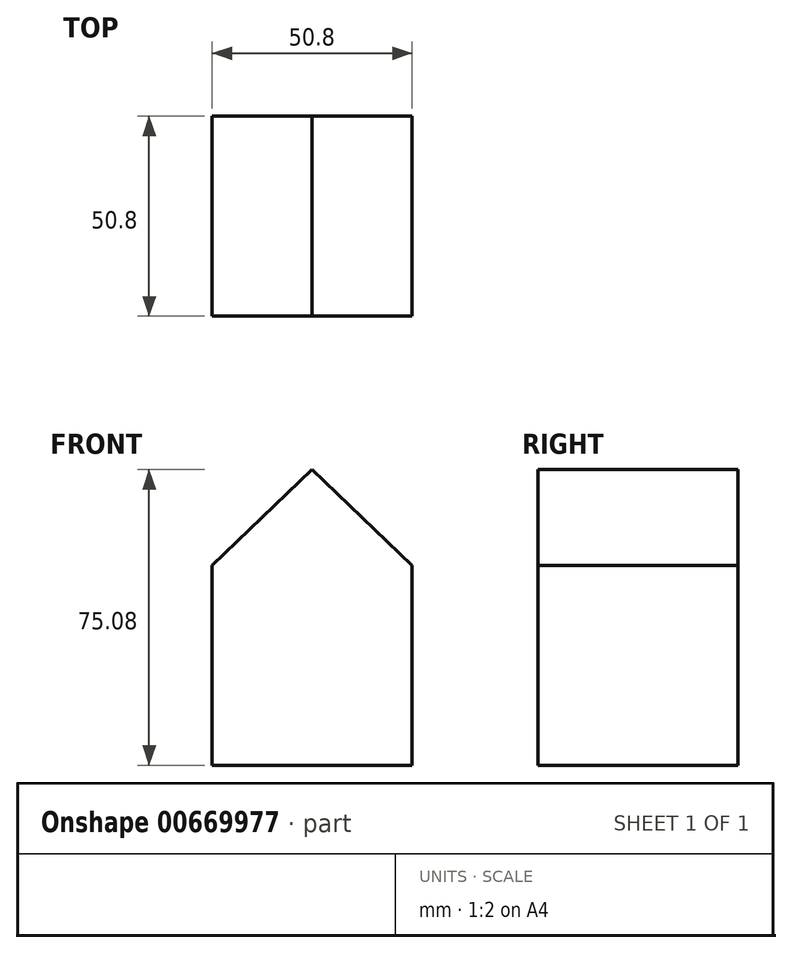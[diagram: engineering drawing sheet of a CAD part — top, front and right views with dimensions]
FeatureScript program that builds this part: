
annotation { "Feature Type Name" : "Feature", "Feature Type Description" : "" }
export const myFeature = defineFeature(function(context is Context, id is Id, definition is map)
    precondition{}
    {
        {
            var Q0;
            Q0=qCreatedBy(makeId("Front.planeOp"),FACE);
            var sketch = newSketch(context, id + "F0", { "sketchPlane" : qUnion([Q0])});
            skLineSegment(sketch, "E0.bottom", {"start": v(25.4, -25.4) * mm, "end": v(-25.4, -25.4) * mm});
            skLineSegment(sketch, "E0.top", {"start": v(25.4, 25.4) * mm, "end": v(-25.4, 25.4) * mm});
            skLineSegment(sketch, "E0.left", {"start": v(25.4, -25.4) * mm, "end": v(25.4, 25.4) * mm});
            skLineSegment(sketch, "E0.right", {"start": v(-25.4, -25.4) * mm, "end": v(-25.4, 25.4) * mm});
            skPoint(sketch, "E0.middle", {"position": v(0, 0) * mm});
            skLineSegment(sketch, "E1", {"start": v(-25.4, 25.4) * mm, "end": v(0, 49.68) * mm});
            skLineSegment(sketch, "E2", {"start": v(0, 49.68) * mm, "end": v(25.4, 25.4) * mm});
            skSolve(sketch);
        }
        {
            var Q0;
            Q0 = qSketchRegion(id + "F0", true);
            extrude(context, id + "F1", {"entities" : qUnion([Q0]), "depth" : 50.8 * mm, "offsetDistance" : 25.4 * mm});
        }
    });
